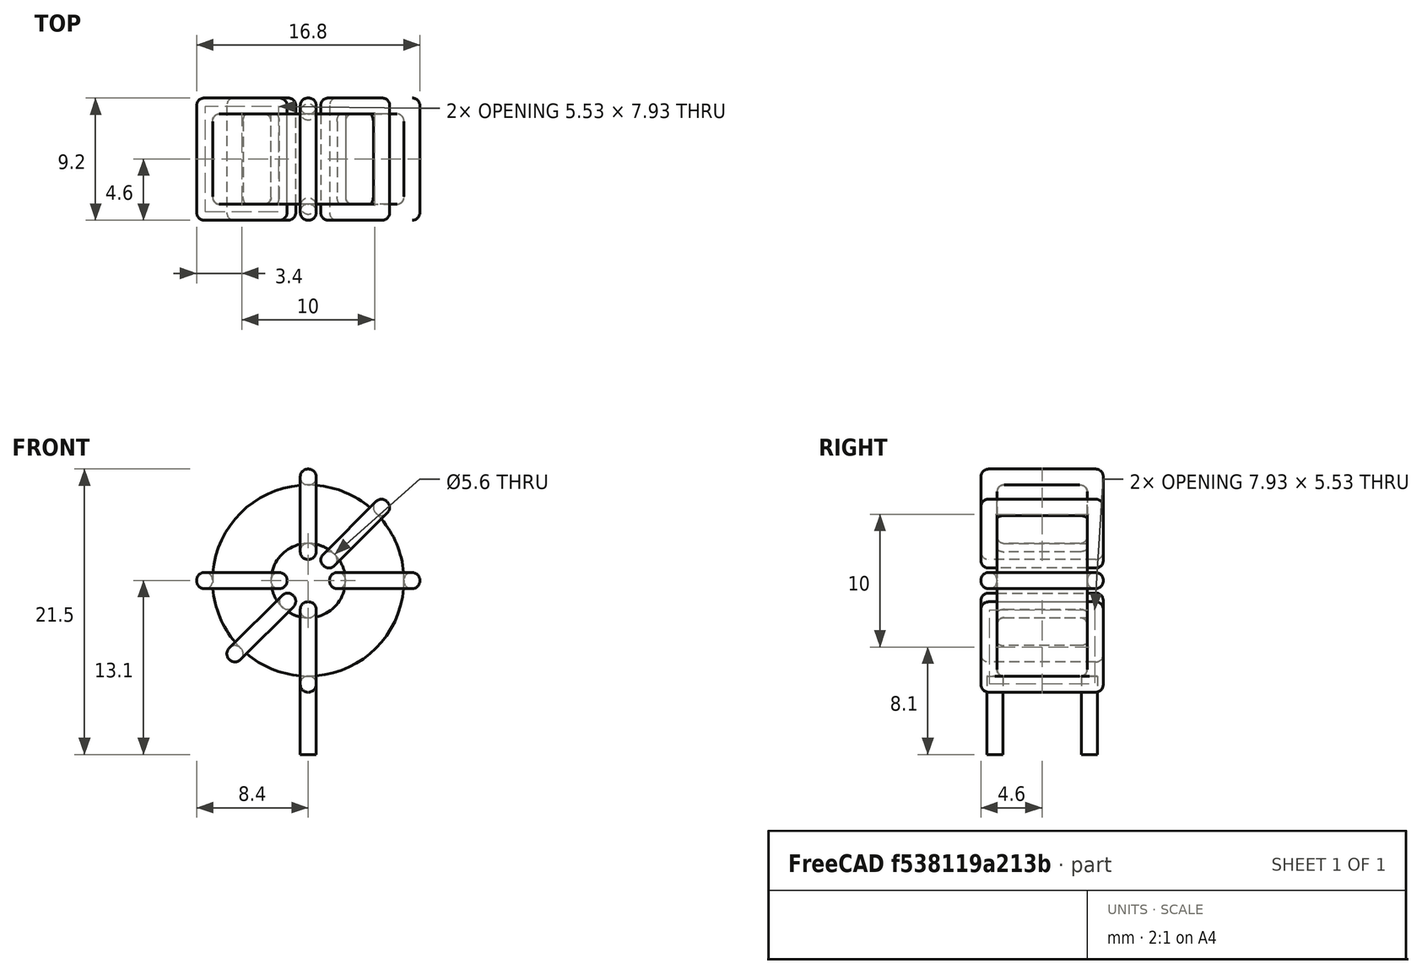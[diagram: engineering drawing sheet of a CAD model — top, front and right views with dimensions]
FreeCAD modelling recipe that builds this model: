
FCSTD DOCUMENT  (FreeCAD 0.16R6703 (Git))
Label: L_Toroid_Vertical_L16.8mm_W9.2mm_P7.10mm_Vishay_TJ3_BigPads
License: All rights reserved
LicenseURL: http://en.wikipedia.org/wiki/All_rights_reserved
objects: Sketcher::SketchObject×6, PartDesign::Pad×6, PartDesign::Fillet×5, Spreadsheet::Sheet×1
note: 23 computed .brp shape members not serialized (recipe doc carries the construction recipe); baked Part::Feature solids carry a one-line shape summary decoded from their .brp

FEATURE [Spreadsheet::Sheet] Spreadsheet  label="dimensions"
  cells = A1=Wx; B1(Wx)=16.8; C1(WW)=5.600000000000001; D1=16.8; A2=Wy; B2(Wy)=9.199999999999999; D2=9.199999999999999; A3=RM; B3(RMx)=7.1; C3(RMy)=0; A4=d_wire; B4(d_wire)=1.2; A5=H; B5(H)=16.8; A6=offsetx; B6(offsetx)=8.4
FEATURE [Sketcher::SketchObject] Sketch
  Placement = pos=(0,-3.55,0) rot=(1,0,0;1.5708rad)
  expr: Placement.Base.y = -Spreadsheet.RMx / 2
  expr: Constraints[0] = Spreadsheet.Wx / 2 - Spreadsheet.d_wire
  expr: Constraints[4] = Spreadsheet.WW / 2
  expr: Constraints[2] = Spreadsheet.Wx / 2 + Spreadsheet.d_wire + 0.5
  sketch-geometry (2):
    g0: Circle CenterX=0 CenterY=10.1 CenterZ=0 NormalX=0 NormalY=0 NormalZ=1 Radius=7.2
    g1: Circle CenterX=0 CenterY=10.1 CenterZ=0 NormalX=0 NormalY=0 NormalZ=1 Radius=2.8
  constraints (5):
    c: Radius(g0) = 7.2
    c: DistanceX(g-1,g0) = 0
    c: DistanceY(g-1,g0) = 10.1
    c: Coincident(g1,g0)
    c: Radius(g1) = 2.8
FEATURE [PartDesign::Pad] Pad
  Length = 6.8
  Length2 = 100
  Midplane = true
  Placement = pos=(0,-3.55,0) rot=(1,0,0;1.5708rad)
  Sketch = -> Sketch
  Type = 0
  expr: Length = Spreadsheet.Wy - 2 * Spreadsheet.d_wire
FEATURE [Sketcher::SketchObject] Sketch001
  Placement = pos=(0,0,1.7) rot=(0,0,1;0rad)
  expr: Placement.Base.z = 0.5 + Spreadsheet.d_wire
  expr: Constraints[4] = Spreadsheet.RMy
  expr: Constraints[2] = -Spreadsheet.RMx
  expr: Constraints[1] = Spreadsheet.d_wire / 2
  sketch-geometry (2):
    g0: Circle CenterX=0 CenterY=0 CenterZ=0 NormalX=0 NormalY=0 NormalZ=1 Radius=0.6
    g1: Circle CenterX=0 CenterY=-7.1 CenterZ=0 NormalX=0 NormalY=0 NormalZ=1 Radius=0.6
  constraints (5):
    c: Equal(g0,g1)
    c: Radius(g0) = 0.6
    c: DistanceY(g-1,g1) = -7.1
    c: Coincident(g0,g-1)
    c: DistanceX(g-1,g1) = 0
FEATURE [PartDesign::Pad] Pad001
  Length = 1.2
  Length2 = 4.7
  Placement = pos=(0,0,1.7) rot=(0,0,1;0rad)
  Reversed = true
  Sketch = -> Sketch001
  Type = 4
  expr: Length2 = 3.5 + Spreadsheet.d_wire
  expr: Length = Spreadsheet.d_wire
FEATURE [PartDesign::Fillet] Fillet
  Base = -> Pad [Edge6,Edge3,Edge2]
  Placement = pos=(0,-3.55,0) rot=(1,0,0;1.5708rad)
  Radius = 0.5
FEATURE [Sketcher::SketchObject] Sketch003
  Placement = pos=(0,1.05,10.1) rot=(1,0,0;3.14159rad)
  expr: Constraints[18] = Spreadsheet.d_wire
  expr: Constraints[16] = Spreadsheet.d_wire
  expr: Constraints[19] = Spreadsheet.d_wire
  expr: Constraints[17] = Spreadsheet.d_wire
  expr: Placement.Base.y = -1 * (Spreadsheet.RMx - Spreadsheet.Wy) / 2
  expr: Constraints[21] = (Spreadsheet.Wx - Spreadsheet.WW) / 2 - Spreadsheet.d_wire
  expr: Constraints[22] = Spreadsheet.Wx / 2 - Spreadsheet.d_wire
  expr: Constraints[43] = Spreadsheet.d_wire
  expr: Constraints[48] = Spreadsheet.Wx - Spreadsheet.d_wire * 2
  expr: Constraints[49] = Spreadsheet.Wy
  expr: Placement.Base.z = Spreadsheet.Wx / 2 + Spreadsheet.d_wire + 0.5
  sketch-geometry (16):
    g0: LineSegment StartX=-1.6 StartY=0 StartZ=0 EndX=-8.4 EndY=0 EndZ=0
    g1: LineSegment StartX=-8.4 StartY=0 StartZ=0 EndX=-8.4 EndY=9.2 EndZ=0
    g2: LineSegment StartX=-8.4 StartY=9.2 StartZ=0 EndX=-1.6 EndY=9.2 EndZ=0
    g3: LineSegment StartX=-1.6 StartY=9.2 StartZ=0 EndX=-1.6 EndY=0 EndZ=0
    g4: LineSegment StartX=-7.2 StartY=8 StartZ=0 EndX=-2.8 EndY=8 EndZ=0
    g5: LineSegment StartX=-2.8 StartY=8 StartZ=0 EndX=-2.8 EndY=1.2 EndZ=0
    g6: LineSegment StartX=-2.8 StartY=1.2 StartZ=0 EndX=-7.2 EndY=1.2 EndZ=0
    g7: LineSegment StartX=-7.2 StartY=1.2 StartZ=0 EndX=-7.2 EndY=8 EndZ=0
    g8: LineSegment StartX=1.6 StartY=9.2 StartZ=0 EndX=8.4 EndY=9.2 EndZ=0
    g9: LineSegment StartX=8.4 StartY=9.2 StartZ=0 EndX=8.4 EndY=0 EndZ=0
    g10: LineSegment StartX=8.4 StartY=0 StartZ=0 EndX=1.6 EndY=0 EndZ=0
    g11: LineSegment StartX=1.6 StartY=0 StartZ=0 EndX=1.6 EndY=9.2 EndZ=0
    g12: LineSegment StartX=2.8 StartY=8 StartZ=0 EndX=7.2 EndY=8 EndZ=0
    g13: LineSegment StartX=7.2 StartY=8 StartZ=0 EndX=7.2 EndY=1.2 EndZ=0
    g14: LineSegment StartX=7.2 StartY=1.2 StartZ=0 EndX=2.8 EndY=1.2 EndZ=0
    g15: LineSegment StartX=2.8 StartY=1.2 StartZ=0 EndX=2.8 EndY=8 EndZ=0
  constraints (50):
    c: Horizontal(g0)
    c: Coincident(g1,g0)
    c: Vertical(g1)
    c: Coincident(g2,g1)
    c: Horizontal(g2)
    c: Coincident(g3,g2)
    c: Coincident(g3,g0)
    c: Vertical(g3)
    c: Coincident(g4,g5)
    c: Coincident(g5,g6)
    c: Coincident(g6,g7)
    c: Coincident(g7,g4)
    c: Horizontal(g4)
    c: Horizontal(g6)
    c: Vertical(g5)
    c: Vertical(g7)
    c: DistanceX(g1,g4) = 1.2
    c: DistanceY(g4,g1) = 1.2
    c: DistanceX(g5,g0) = 1.2
    c: DistanceY(g0,g5) = 1.2
    c: DistanceY(g-1,g0) = 0
    c: DistanceX(g6,g6) = 4.4
    c: DistanceX(g6,g-1) = 7.2
    c: Coincident(g8,g9)
    c: Coincident(g9,g10)
    c: Coincident(g10,g11)
    c: Coincident(g11,g8)
    c: Horizontal(g8)
    c: Horizontal(g10)
    c: Vertical(g9)
    c: Vertical(g11)
    c: Coincident(g12,g13)
    c: Coincident(g13,g14)
    c: Coincident(g14,g15)
    c: Coincident(g15,g12)
    c: Horizontal(g12)
    c: Horizontal(g14)
    c: Vertical(g13)
    c: Vertical(g15)
    c: DistanceY(g8,g2) = 0
    c: DistanceY(g10,g0) = 0
    c: DistanceY(g14,g5) = 0
    c: DistanceY(g12,g4) = 0
    c: DistanceX(g8,g12) = 1.2
    c: Equal(g8,g2)
    c: Equal(g12,g4)
    c: Equal(g9,g1)
    c: Equal(g13,g7)
    c: DistanceX(g4,g12) = 14.4
    c: DistanceY(g0,g1) = 9.2
FEATURE [PartDesign::Pad] Pad002
  Length = 1.2
  Length2 = 100
  Midplane = true
  Placement = pos=(0,1.05,10.1) rot=(1,0,0;3.14159rad)
  Sketch = -> Sketch003
  Type = 0
  expr: Length = Spreadsheet.d_wire
FEATURE [PartDesign::Fillet] Fillet001
  Base = -> Pad002 [Edge38,Edge41,Edge42,Edge43,Edge29,Edge32,Edge33,Edge34,Edge25,Edge35,Edge36,Edge13,Edge14,Edge15,Edge16,Edge17,Edge18,Edge19,Edge1,Edge2,Edge3,Edge4,Edge5,Edge6,Edge7,Edge37,Edge39,Edge40,Edge20,Edge23,Edge24,Edge21,Edge22,Edge8,Edge9,Edge10,Edge11,Edge12,Edge26,Edge27,+8 more]
  Placement = pos=(0,1.05,10.1) rot=(1,0,0;3.14159rad)
  Radius = 0.564
  expr: Radius = Spreadsheet.d_wire * 0.47
FEATURE [Sketcher::SketchObject] Sketch004
  Placement = pos=(0,1.05,10.1) rot=(0.92388,0,0.382683;3.14159rad)
  expr: Constraints[18] = Spreadsheet.d_wire
  expr: Constraints[16] = Spreadsheet.d_wire
  expr: Constraints[19] = Spreadsheet.d_wire
  expr: Constraints[17] = Spreadsheet.d_wire
  expr: Placement.Base.y = -1 * (Spreadsheet.RMx - Spreadsheet.Wy) / 2
  expr: Constraints[21] = (Spreadsheet.Wx - Spreadsheet.WW) / 2 - Spreadsheet.d_wire
  expr: Constraints[22] = Spreadsheet.Wx / 2 - Spreadsheet.d_wire
  expr: Constraints[43] = Spreadsheet.d_wire
  expr: Constraints[48] = Spreadsheet.Wx - 2 * Spreadsheet.d_wire
  expr: Constraints[49] = Spreadsheet.Wy
  expr: Placement.Base.z = Spreadsheet.Wx / 2 + Spreadsheet.d_wire + 0.5
  sketch-geometry (16):
    g0: LineSegment StartX=-1.6 StartY=0 StartZ=0 EndX=-8.4 EndY=0 EndZ=0
    g1: LineSegment StartX=-8.4 StartY=0 StartZ=0 EndX=-8.4 EndY=9.2 EndZ=0
    g2: LineSegment StartX=-8.4 StartY=9.2 StartZ=0 EndX=-1.6 EndY=9.2 EndZ=0
    g3: LineSegment StartX=-1.6 StartY=9.2 StartZ=0 EndX=-1.6 EndY=0 EndZ=0
    g4: LineSegment StartX=-7.2 StartY=8 StartZ=0 EndX=-2.8 EndY=8 EndZ=0
    g5: LineSegment StartX=-2.8 StartY=8 StartZ=0 EndX=-2.8 EndY=1.2 EndZ=0
    g6: LineSegment StartX=-2.8 StartY=1.2 StartZ=0 EndX=-7.2 EndY=1.2 EndZ=0
    g7: LineSegment StartX=-7.2 StartY=1.2 StartZ=0 EndX=-7.2 EndY=8 EndZ=0
    g8: LineSegment StartX=1.6 StartY=9.2 StartZ=0 EndX=8.4 EndY=9.2 EndZ=0
    g9: LineSegment StartX=8.4 StartY=9.2 StartZ=0 EndX=8.4 EndY=0 EndZ=0
    g10: LineSegment StartX=8.4 StartY=0 StartZ=0 EndX=1.6 EndY=0 EndZ=0
    g11: LineSegment StartX=1.6 StartY=0 StartZ=0 EndX=1.6 EndY=9.2 EndZ=0
    g12: LineSegment StartX=2.8 StartY=8 StartZ=0 EndX=7.2 EndY=8 EndZ=0
    g13: LineSegment StartX=7.2 StartY=8 StartZ=0 EndX=7.2 EndY=1.2 EndZ=0
    g14: LineSegment StartX=7.2 StartY=1.2 StartZ=0 EndX=2.8 EndY=1.2 EndZ=0
    g15: LineSegment StartX=2.8 StartY=1.2 StartZ=0 EndX=2.8 EndY=8 EndZ=0
  constraints (50):
    c: Horizontal(g0)
    c: Coincident(g1,g0)
    c: Vertical(g1)
    c: Coincident(g2,g1)
    c: Horizontal(g2)
    c: Coincident(g3,g2)
    c: Coincident(g3,g0)
    c: Vertical(g3)
    c: Coincident(g4,g5)
    c: Coincident(g5,g6)
    c: Coincident(g6,g7)
    c: Coincident(g7,g4)
    c: Horizontal(g4)
    c: Horizontal(g6)
    c: Vertical(g5)
    c: Vertical(g7)
    c: DistanceX(g1,g4) = 1.2
    c: DistanceY(g4,g1) = 1.2
    c: DistanceX(g5,g0) = 1.2
    c: DistanceY(g0,g5) = 1.2
    c: DistanceY(g-1,g0) = 0
    c: DistanceX(g6,g6) = 4.4
    c: DistanceX(g6,g-1) = 7.2
    c: Coincident(g8,g9)
    c: Coincident(g9,g10)
    c: Coincident(g10,g11)
    c: Coincident(g11,g8)
    c: Horizontal(g8)
    c: Horizontal(g10)
    c: Vertical(g9)
    c: Vertical(g11)
    c: Coincident(g12,g13)
    c: Coincident(g13,g14)
    c: Coincident(g14,g15)
    c: Coincident(g15,g12)
    c: Horizontal(g12)
    c: Horizontal(g14)
    c: Vertical(g13)
    c: Vertical(g15)
    c: DistanceY(g8,g2) = 0
    c: DistanceY(g10,g0) = 0
    c: DistanceY(g14,g5) = 0
    c: DistanceY(g12,g4) = 0
    c: DistanceX(g8,g12) = 1.2
    c: Equal(g8,g2)
    c: Equal(g12,g4)
    c: Equal(g9,g1)
    c: Equal(g13,g7)
    c: DistanceX(g4,g12) = 14.4
    c: DistanceY(g0,g1) = 9.2
FEATURE [PartDesign::Pad] Pad003
  Length = 1.2
  Length2 = 100
  Midplane = true
  Placement = pos=(0,1.05,10.1) rot=(0.92388,0,0.382683;3.14159rad)
  Sketch = -> Sketch004
  Type = 0
  expr: Length = Spreadsheet.d_wire
FEATURE [PartDesign::Fillet] Fillet002
  Base = -> Pad003 [Edge38,Edge41,Edge42,Edge43,Edge29,Edge32,Edge33,Edge34,Edge25,Edge35,Edge36,Edge13,Edge14,Edge15,Edge16,Edge17,Edge18,Edge19,Edge1,Edge2,Edge3,Edge4,Edge5,Edge6,Edge7,Edge37,Edge39,Edge40,Edge20,Edge23,Edge24,Edge21,Edge22,Edge8,Edge9,Edge10,Edge11,Edge12,Edge26,Edge27,+8 more]
  Placement = pos=(0,1.05,10.1) rot=(0.92388,0,0.382683;3.14159rad)
  Radius = 0.564
  expr: Radius = Spreadsheet.d_wire * 0.47
FEATURE [Sketcher::SketchObject] Sketch005
  Placement = pos=(0,1.05,10.1) rot=(0.92388,0,-0.382683;3.14159rad)
  expr: Constraints[18] = Spreadsheet.d_wire
  expr: Constraints[16] = Spreadsheet.d_wire
  expr: Constraints[19] = Spreadsheet.d_wire
  expr: Constraints[17] = Spreadsheet.d_wire
  expr: Placement.Base.y = -1 * (Spreadsheet.RMx - Spreadsheet.Wy) / 2
  expr: Constraints[21] = (Spreadsheet.Wx - Spreadsheet.WW) / 2 - Spreadsheet.d_wire
  expr: Constraints[22] = Spreadsheet.Wx / 2 - Spreadsheet.d_wire
  expr: Constraints[43] = Spreadsheet.d_wire
  expr: Constraints[48] = Spreadsheet.Wx - 2 * Spreadsheet.d_wire
  expr: Constraints[49] = Spreadsheet.Wy
  expr: Placement.Base.z = Spreadsheet.Wx / 2 + Spreadsheet.d_wire + 0.5
  sketch-geometry (16):
    g0: LineSegment StartX=-1.6 StartY=0 StartZ=0 EndX=-8.4 EndY=0 EndZ=0
    g1: LineSegment StartX=-8.4 StartY=0 StartZ=0 EndX=-8.4 EndY=9.2 EndZ=0
    g2: LineSegment StartX=-8.4 StartY=9.2 StartZ=0 EndX=-1.6 EndY=9.2 EndZ=0
    g3: LineSegment StartX=-1.6 StartY=9.2 StartZ=0 EndX=-1.6 EndY=0 EndZ=0
    g4: LineSegment StartX=-7.2 StartY=8 StartZ=0 EndX=-2.8 EndY=8 EndZ=0
    g5: LineSegment StartX=-2.8 StartY=8 StartZ=0 EndX=-2.8 EndY=1.2 EndZ=0
    g6: LineSegment StartX=-2.8 StartY=1.2 StartZ=0 EndX=-7.2 EndY=1.2 EndZ=0
    g7: LineSegment StartX=-7.2 StartY=1.2 StartZ=0 EndX=-7.2 EndY=8 EndZ=0
    g8: LineSegment StartX=1.6 StartY=9.2 StartZ=0 EndX=8.4 EndY=9.2 EndZ=0
    g9: LineSegment StartX=8.4 StartY=9.2 StartZ=0 EndX=8.4 EndY=0 EndZ=0
    g10: LineSegment StartX=8.4 StartY=0 StartZ=0 EndX=1.6 EndY=0 EndZ=0
    g11: LineSegment StartX=1.6 StartY=0 StartZ=0 EndX=1.6 EndY=9.2 EndZ=0
    g12: LineSegment StartX=2.8 StartY=8 StartZ=0 EndX=7.2 EndY=8 EndZ=0
    g13: LineSegment StartX=7.2 StartY=8 StartZ=0 EndX=7.2 EndY=1.2 EndZ=0
    g14: LineSegment StartX=7.2 StartY=1.2 StartZ=0 EndX=2.8 EndY=1.2 EndZ=0
    g15: LineSegment StartX=2.8 StartY=1.2 StartZ=0 EndX=2.8 EndY=8 EndZ=0
  constraints (50):
    c: Horizontal(g0)
    c: Coincident(g1,g0)
    c: Vertical(g1)
    c: Coincident(g2,g1)
    c: Horizontal(g2)
    c: Coincident(g3,g2)
    c: Coincident(g3,g0)
    c: Vertical(g3)
    c: Coincident(g4,g5)
    c: Coincident(g5,g6)
    c: Coincident(g6,g7)
    c: Coincident(g7,g4)
    c: Horizontal(g4)
    c: Horizontal(g6)
    c: Vertical(g5)
    c: Vertical(g7)
    c: DistanceX(g1,g4) = 1.2
    c: DistanceY(g4,g1) = 1.2
    c: DistanceX(g5,g0) = 1.2
    c: DistanceY(g0,g5) = 1.2
    c: DistanceY(g-1,g0) = 0
    c: DistanceX(g6,g6) = 4.4
    c: DistanceX(g6,g-1) = 7.2
    c: Coincident(g8,g9)
    c: Coincident(g9,g10)
    c: Coincident(g10,g11)
    c: Coincident(g11,g8)
    c: Horizontal(g8)
    c: Horizontal(g10)
    c: Vertical(g9)
    c: Vertical(g11)
    c: Coincident(g12,g13)
    c: Coincident(g13,g14)
    c: Coincident(g14,g15)
    c: Coincident(g15,g12)
    c: Horizontal(g12)
    c: Horizontal(g14)
    c: Vertical(g13)
    c: Vertical(g15)
    c: DistanceY(g8,g2) = 0
    c: DistanceY(g10,g0) = 0
    c: DistanceY(g14,g5) = 0
    c: DistanceY(g12,g4) = 0
    c: DistanceX(g8,g12) = 1.2
    c: Equal(g8,g2)
    c: Equal(g12,g4)
    c: Equal(g9,g1)
    c: Equal(g13,g7)
    c: DistanceX(g4,g12) = 14.4
    c: DistanceY(g0,g1) = 9.2
FEATURE [PartDesign::Pad] Pad004
  Length = 1.2
  Length2 = 100
  Midplane = true
  Placement = pos=(0,1.05,10.1) rot=(0.92388,0,-0.382683;3.14159rad)
  Sketch = -> Sketch005
  Type = 0
  expr: Length = Spreadsheet.d_wire
FEATURE [PartDesign::Fillet] Fillet003
  Base = -> Pad004 [Edge38,Edge41,Edge42,Edge43,Edge29,Edge32,Edge33,Edge34,Edge25,Edge35,Edge36,Edge13,Edge14,Edge15,Edge16,Edge17,Edge18,Edge19,Edge1,Edge2,Edge3,Edge4,Edge5,Edge6,Edge7,Edge37,Edge39,Edge40,Edge20,Edge23,Edge24,Edge21,Edge22,Edge8,Edge9,Edge10,Edge11,Edge12,Edge26,Edge27,+8 more]
  Placement = pos=(0,1.05,10.1) rot=(0.92388,0,-0.382683;3.14159rad)
  Radius = 0.564
  expr: Radius = Spreadsheet.d_wire * 0.47
FEATURE [Sketcher::SketchObject] Sketch006
  Placement = pos=(0,1.05,10.1) rot=(0.707107,0,0.707107;3.14159rad)
  expr: Constraints[18] = Spreadsheet.d_wire
  expr: Constraints[16] = Spreadsheet.d_wire
  expr: Constraints[19] = Spreadsheet.d_wire
  expr: Constraints[17] = Spreadsheet.d_wire
  expr: Placement.Base.y = -1 * (Spreadsheet.RMx - Spreadsheet.Wy) / 2
  expr: Constraints[21] = (Spreadsheet.Wx - Spreadsheet.WW) / 2 - Spreadsheet.d_wire
  expr: Constraints[22] = Spreadsheet.Wx / 2 - Spreadsheet.d_wire
  expr: Constraints[43] = Spreadsheet.d_wire
  expr: Constraints[48] = Spreadsheet.Wx - Spreadsheet.d_wire * 2
  expr: Constraints[49] = Spreadsheet.Wy
  expr: Placement.Base.z = Spreadsheet.Wx / 2 + Spreadsheet.d_wire + 0.5
  sketch-geometry (16):
    g0: LineSegment StartX=-1.6 StartY=0 StartZ=0 EndX=-8.4 EndY=0 EndZ=0
    g1: LineSegment StartX=-8.4 StartY=0 StartZ=0 EndX=-8.4 EndY=9.2 EndZ=0
    g2: LineSegment StartX=-8.4 StartY=9.2 StartZ=0 EndX=-1.6 EndY=9.2 EndZ=0
    g3: LineSegment StartX=-1.6 StartY=9.2 StartZ=0 EndX=-1.6 EndY=0 EndZ=0
    g4: LineSegment StartX=-7.2 StartY=8 StartZ=0 EndX=-2.8 EndY=8 EndZ=0
    g5: LineSegment StartX=-2.8 StartY=8 StartZ=0 EndX=-2.8 EndY=1.2 EndZ=0
    g6: LineSegment StartX=-2.8 StartY=1.2 StartZ=0 EndX=-7.2 EndY=1.2 EndZ=0
    g7: LineSegment StartX=-7.2 StartY=1.2 StartZ=0 EndX=-7.2 EndY=8 EndZ=0
    g8: LineSegment StartX=1.6 StartY=9.2 StartZ=0 EndX=8.4 EndY=9.2 EndZ=0
    g9: LineSegment StartX=8.4 StartY=9.2 StartZ=0 EndX=8.4 EndY=0 EndZ=0
    g10: LineSegment StartX=8.4 StartY=0 StartZ=0 EndX=1.6 EndY=0 EndZ=0
    g11: LineSegment StartX=1.6 StartY=0 StartZ=0 EndX=1.6 EndY=9.2 EndZ=0
    g12: LineSegment StartX=2.8 StartY=8 StartZ=0 EndX=7.2 EndY=8 EndZ=0
    g13: LineSegment StartX=7.2 StartY=8 StartZ=0 EndX=7.2 EndY=1.2 EndZ=0
    g14: LineSegment StartX=7.2 StartY=1.2 StartZ=0 EndX=2.8 EndY=1.2 EndZ=0
    g15: LineSegment StartX=2.8 StartY=1.2 StartZ=0 EndX=2.8 EndY=8 EndZ=0
  constraints (50):
    c: Horizontal(g0)
    c: Coincident(g1,g0)
    c: Vertical(g1)
    c: Coincident(g2,g1)
    c: Horizontal(g2)
    c: Coincident(g3,g2)
    c: Coincident(g3,g0)
    c: Vertical(g3)
    c: Coincident(g4,g5)
    c: Coincident(g5,g6)
    c: Coincident(g6,g7)
    c: Coincident(g7,g4)
    c: Horizontal(g4)
    c: Horizontal(g6)
    c: Vertical(g5)
    c: Vertical(g7)
    c: DistanceX(g1,g4) = 1.2
    c: DistanceY(g4,g1) = 1.2
    c: DistanceX(g5,g0) = 1.2
    c: DistanceY(g0,g5) = 1.2
    c: DistanceY(g-1,g0) = 0
    c: DistanceX(g6,g6) = 4.4
    c: DistanceX(g6,g-1) = 7.2
    c: Coincident(g8,g9)
    c: Coincident(g9,g10)
    c: Coincident(g10,g11)
    c: Coincident(g11,g8)
    c: Horizontal(g8)
    c: Horizontal(g10)
    c: Vertical(g9)
    c: Vertical(g11)
    c: Coincident(g12,g13)
    c: Coincident(g13,g14)
    c: Coincident(g14,g15)
    c: Coincident(g15,g12)
    c: Horizontal(g12)
    c: Horizontal(g14)
    c: Vertical(g13)
    c: Vertical(g15)
    c: DistanceY(g8,g2) = 0
    c: DistanceY(g10,g0) = 0
    c: DistanceY(g14,g5) = 0
    c: DistanceY(g12,g4) = 0
    c: DistanceX(g8,g12) = 1.2
    c: Equal(g8,g2)
    c: Equal(g12,g4)
    c: Equal(g9,g1)
    c: Equal(g13,g7)
    c: DistanceX(g4,g12) = 14.4
    c: DistanceY(g0,g1) = 9.2
FEATURE [PartDesign::Pad] Pad005
  Length = 1.2
  Length2 = 100
  Midplane = true
  Placement = pos=(0,1.05,10.1) rot=(0.707107,0,0.707107;3.14159rad)
  Sketch = -> Sketch006
  Type = 0
  expr: Length = Spreadsheet.d_wire
FEATURE [PartDesign::Fillet] Fillet004
  Base = -> Pad005 [Edge38,Edge41,Edge42,Edge43,Edge29,Edge32,Edge33,Edge34,Edge25,Edge35,Edge36,Edge13,Edge14,Edge15,Edge16,Edge17,Edge18,Edge19,Edge1,Edge2,Edge3,Edge4,Edge5,Edge6,Edge7,Edge37,Edge39,Edge40,Edge20,Edge23,Edge24,Edge21,Edge22,Edge8,Edge9,Edge10,Edge11,Edge12,Edge26,Edge27,+8 more]
  Placement = pos=(0,1.05,10.1) rot=(0.707107,0,0.707107;3.14159rad)
  Radius = 0.564
  expr: Radius = Spreadsheet.d_wire * 0.47
